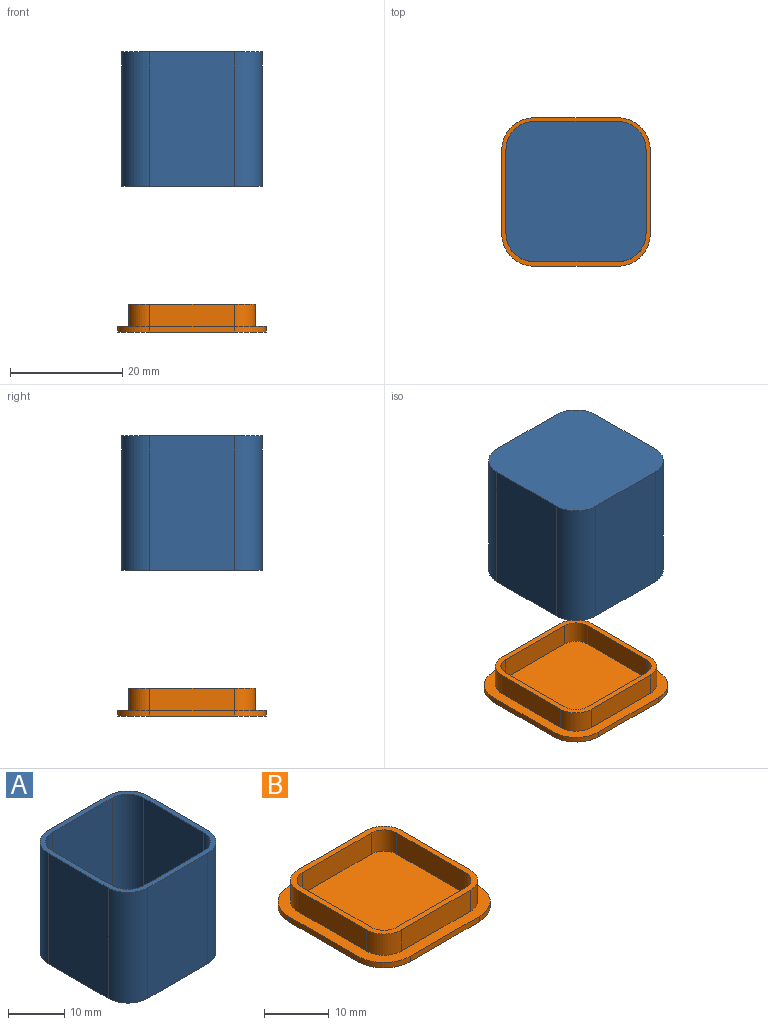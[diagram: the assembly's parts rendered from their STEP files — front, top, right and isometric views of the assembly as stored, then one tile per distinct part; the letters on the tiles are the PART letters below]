
ASSEMBLY  parts=2 mates=1
PART A: 19 faces, bbox 25x25x24 mm
  f0: cylinder r=5mm len=24mm, axis (0,0,-1), area 188.5mm2, adj f1,f7,f8,f17
  f1: plane 24x15mm, normal (0,-1,0), area 360mm2, adj f0,f2,f8,f17
  f2: cylinder r=5mm len=24mm, axis (0,0,-1), area 188.5mm2, adj f1,f3,f8,f17
  f3: plane 24x15mm, normal (1,0,0), area 360mm2, adj f2,f4,f8,f17
  f4: cylinder r=5mm len=24mm, axis (0,0,-1), area 188.5mm2, adj f3,f5,f8,f17
  f5: plane 24x15mm, normal (0,1,0), area 360mm2, adj f4,f6,f8,f17
  f6: cylinder r=5mm len=24mm, axis (0,0,-1), area 188.5mm2, adj f5,f7,f8,f17
  f7: plane 24x15mm, normal (-1,0,0), area 360mm2, adj f0,f6,f8,f17
  f8: plane 25x25mm, normal (0,0,-1), area 603.5mm2, adj f0,f1,f2,f3,f4,f5,f6,f7
  f9: plane 23x15mm, normal (0,1,0), area 345mm2, adj f10,f16,f17,f18
  f10: cylinder r=4mm len=23mm, axis (0,0,-1), area 144.5mm2, adj f9,f11,f17,f18
  f11: plane 23x15mm, normal (1,0,0), area 345mm2, adj f10,f12,f17,f18
  f12: cylinder r=4mm len=23mm, axis (0,0,-1), area 144.5mm2, adj f11,f13,f17,f18
  f13: plane 23x15mm, normal (0,-1,0), area 345mm2, adj f12,f14,f17,f18
  f14: cylinder r=4mm len=23mm, axis (0,0,-1), area 144.5mm2, adj f13,f15,f17,f18
  f15: plane 23x15mm, normal (-1,0,0), area 345mm2, adj f14,f16,f17,f18
  f16: cylinder r=4mm len=23mm, axis (0,0,-1), area 144.5mm2, adj f9,f15,f17,f18
  f17: plane 25x25mm, normal (0,0,1), area 88.3mm2, adj f0,f1,f2,f3,f4,f5,f6,f7
  f18: plane 23x23mm, normal (0,0,1), area 515.3mm2, adj f9,f10,f11,f12,f13,f14,f15,f16
PART B: 28 faces, bbox 26.5x26.5x5 mm
  f0: plane 26.5x26.5mm, normal (0,0,1), area 175.5mm2, adj f1,f2,f3,f4,f5,f6,f7,f8
  f1: cylinder r=5.75mm len=5.75mm, axis (0,0,-1), area 9mm2, adj f0,f2,f8,f9
  f2: plane 15x1mm, normal (0,-1,0), area 15mm2, adj f0,f1,f3,f9
  f3: cylinder r=5.75mm len=5.75mm, axis (0,0,-1), area 9mm2, adj f0,f2,f4,f9
  f4: plane 15x1mm, normal (1,0,0), area 15mm2, adj f0,f3,f5,f9
  f5: cylinder r=5.75mm len=5.75mm, axis (0,0,-1), area 9mm2, adj f0,f4,f6,f9
  f6: plane 15x1mm, normal (0,1,0), area 15mm2, adj f0,f5,f7,f9
  f7: cylinder r=5.75mm len=5.75mm, axis (0,0,-1), area 9mm2, adj f0,f6,f8,f9
  f8: plane 15x1mm, normal (-1,0,0), area 15mm2, adj f0,f1,f7,f9
  f9: plane 26.5x26.5mm, normal (0,0,-1), area 673.9mm2, adj f1,f2,f3,f4,f5,f6,f7,f8
  f10: cylinder r=3.8mm len=4mm, axis (0,0,-1), area 23.9mm2, adj f0,f11,f25,f26
  f11: plane 15x4mm, normal (0,-1,0), area 60mm2, adj f0,f10,f12,f26
  f12: cylinder r=3.8mm len=4mm, axis (0,0,-1), area 23.9mm2, adj f0,f11,f13,f26
  f13: plane 15x4mm, normal (1,0,0), area 60mm2, adj f0,f12,f14,f26
  f14: cylinder r=3.8mm len=4mm, axis (0,0,-1), area 23.9mm2, adj f0,f13,f15,f26
  f15: plane 15x4mm, normal (0,1,0), area 60mm2, adj f0,f14,f16,f26
  f16: cylinder r=3.8mm len=4mm, axis (0,0,-1), area 23.9mm2, adj f0,f15,f25,f26
  f17: plane 15x4mm, normal (0,1,0), area 60mm2, adj f18,f24,f26,f27
  f18: cylinder r=2.8mm len=4mm, axis (0,0,-1), area 17.6mm2, adj f17,f19,f26,f27
  f19: plane 15x4mm, normal (1,0,0), area 60mm2, adj f18,f20,f26,f27
  f20: cylinder r=2.8mm len=4mm, axis (0,0,-1), area 17.6mm2, adj f19,f21,f26,f27
  f21: plane 15x4mm, normal (0,-1,0), area 60mm2, adj f20,f22,f26,f27
  f22: cylinder r=2.8mm len=4mm, axis (0,0,-1), area 17.6mm2, adj f21,f23,f26,f27
  f23: plane 15x4mm, normal (-1,0,0), area 60mm2, adj f22,f24,f26,f27
  f24: cylinder r=2.8mm len=4mm, axis (0,0,-1), area 17.6mm2, adj f17,f23,f26,f27
  f25: plane 15x4mm, normal (-1,0,0), area 60mm2, adj f0,f10,f16,f26
  f26: plane 22.6x22.6mm, normal (0,0,1), area 80.7mm2, adj f10,f11,f12,f13,f14,f15,f16,f17
  f27: plane 20.6x20.6mm, normal (0,0,1), area 417.6mm2, adj f17,f18,f19,f20,f21,f22,f23,f24
PLACE A rot(axis=(1,0,0),180deg) t=(5.91,-5.16,2.25)mm fixed
PLACE B t=(5.91,1.63,-47.75)mm
MATE slider B.f27 <-> A.f17  axis (0,0,1) through (5.06,-1.77,-46.75)mm
